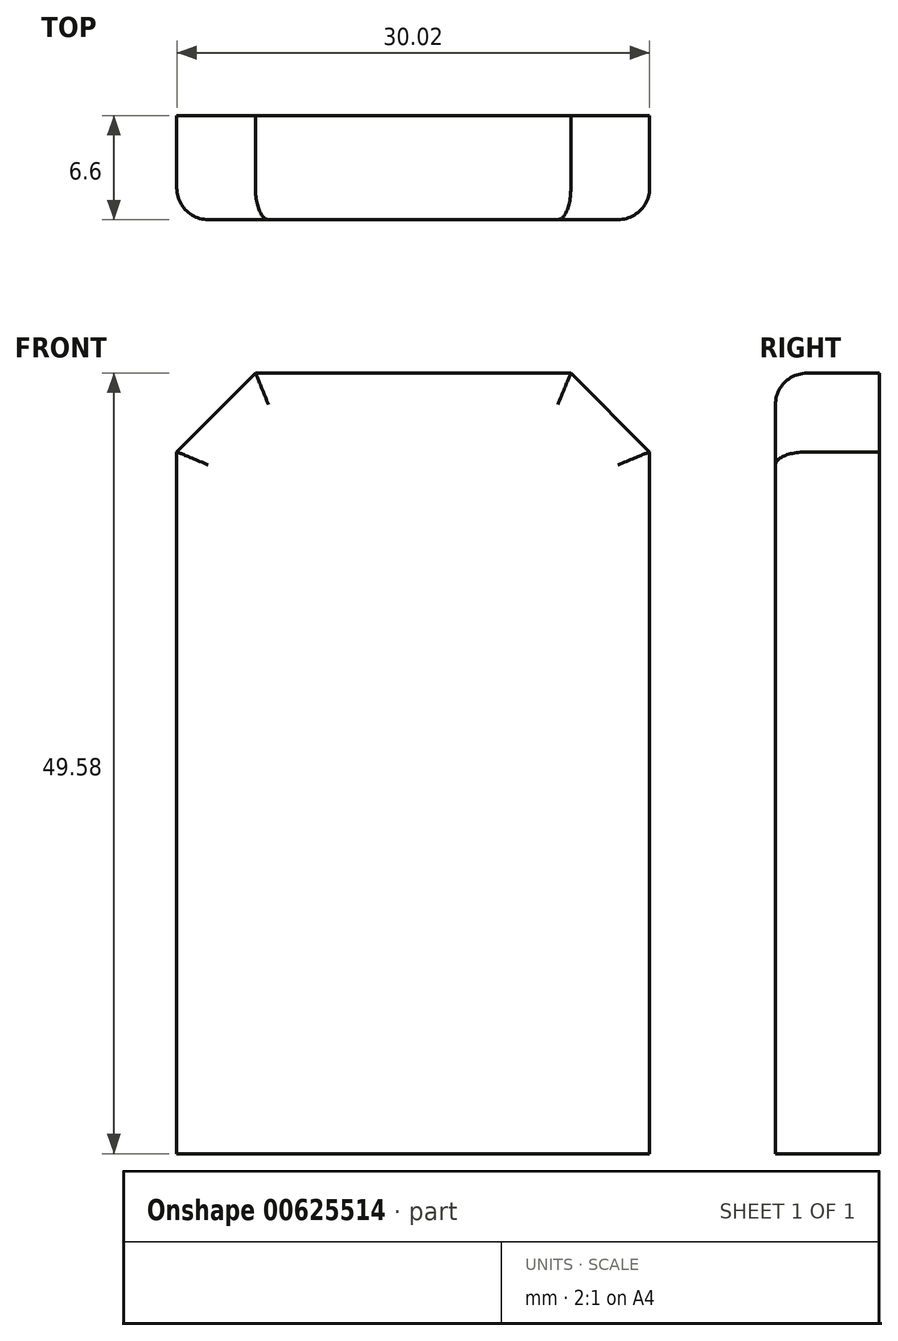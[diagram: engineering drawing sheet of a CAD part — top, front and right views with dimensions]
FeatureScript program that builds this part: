
annotation { "Feature Type Name" : "Feature", "Feature Type Description" : "" }
export const myFeature = defineFeature(function(context is Context, id is Id, definition is map)
    precondition{}
    {
        {
            var Q0;
            Q0=qCreatedBy(makeId("Front.planeOp"),FACE);
            var sketch = newSketch(context, id + "F0", { "sketchPlane" : qUnion([Q0])});
            skLineSegment(sketch, "E0.bottom", {"start": v(15.01, -24.79) * mm, "end": v(-15.01, -24.79) * mm});
            skLineSegment(sketch, "E0.top", {"start": v(15.01, 24.79) * mm, "end": v(-15.01, 24.79) * mm});
            skLineSegment(sketch, "E0.left", {"start": v(15.01, -24.79) * mm, "end": v(15.01, 24.79) * mm});
            skLineSegment(sketch, "E0.right", {"start": v(-15.01, -24.79) * mm, "end": v(-15.01, 24.79) * mm});
            skPoint(sketch, "E0.middle", {"position": v(0, 0) * mm});
            skSolve(sketch);
        }
        {
            var Q0;
            Q0 = qSketchRegion(id + "F0", true);
            extrude(context, id + "F1", {"entities" : qUnion([Q0]), "depth" : 6.6 * mm, "offsetDistance" : 25 * mm});
        }
        {
            var Q0;
            Q0=makeQuery(id+"F1.opExtrude","SWEPT_EDGE",EDGE,{"disambiguationData":[OSD([sQuery(id+"F0.wireOp",EDGE,"E0.top"),sQuery(id+"F0.wireOp",EDGE,"E0.right")])]});
            var Q1;
            Q1=makeQuery(id+"F1.opExtrude","SWEPT_EDGE",EDGE,{"disambiguationData":[OSD([sQuery(id+"F0.wireOp",EDGE,"E0.top"),sQuery(id+"F0.wireOp",EDGE,"E0.left")])]});
            chamfer(context, id + "F2", {"entities" : qUnion([Q0, Q1]), "width" : 5 * mm, "tangentPropagation" : true});
        }
        {
            var Q0;
            {var subQ0=sQuery(id+"F0.wireOp",EDGE,"E0.left");var subQ1=sQuery(id+"F0.wireOp",EDGE,"E0.top");Q0=makeQuery(id+"F2.opChamfer","BLEND_EDGE",EDGE,{"blendedFrom":[makeQuery(id+"F1.opExtrude","SWEPT_EDGE",EDGE,{"disambiguationData":[OSD([subQ1,subQ0])]}),makeQuery(id+"F1.opExtrude","CAP_FACE",FACE,{"disambiguationData":[OSD([sQuery(id+"F0.wireOp",EDGE,"E0.bottom"),subQ1,subQ0,sQuery(id+"F0.wireOp",EDGE,"E0.right")])],"isStart":false})],"blendedInto":[makeQuery(id+"F1.opExtrude","CAP_FACE",FACE,{"disambiguationData":[OSD([sQuery(id+"F0.wireOp",EDGE,"E0.bottom"),subQ1,subQ0,sQuery(id+"F0.wireOp",EDGE,"E0.right")])],"isStart":false})]});}
            var Q1;
            Q1=makeQuery(id+"F1.opExtrude","CAP_EDGE",EDGE,{"disambiguationData":[OSD([sQuery(id+"F0.wireOp",EDGE,"E0.right")])],"isStart":false});
            var Q2;
            Q2=makeQuery(id+"F1.opExtrude","CAP_EDGE",EDGE,{"disambiguationData":[OSD([sQuery(id+"F0.wireOp",EDGE,"E0.top")])],"isStart":false});
            var Q3;
            Q3=makeQuery(id+"F1.opExtrude","CAP_EDGE",EDGE,{"disambiguationData":[OSD([sQuery(id+"F0.wireOp",EDGE,"E0.left")])],"isStart":false});
            var Q4;
            {var subQ0=sQuery(id+"F0.wireOp",EDGE,"E0.right");var subQ1=sQuery(id+"F0.wireOp",EDGE,"E0.top");Q4=makeQuery(id+"F2.opChamfer","BLEND_EDGE",EDGE,{"blendedFrom":[makeQuery(id+"F1.opExtrude","SWEPT_EDGE",EDGE,{"disambiguationData":[OSD([subQ1,subQ0])]}),makeQuery(id+"F1.opExtrude","CAP_FACE",FACE,{"disambiguationData":[OSD([sQuery(id+"F0.wireOp",EDGE,"E0.bottom"),subQ1,sQuery(id+"F0.wireOp",EDGE,"E0.left"),subQ0])],"isStart":false})],"blendedInto":[makeQuery(id+"F1.opExtrude","CAP_FACE",FACE,{"disambiguationData":[OSD([sQuery(id+"F0.wireOp",EDGE,"E0.bottom"),subQ1,sQuery(id+"F0.wireOp",EDGE,"E0.left"),subQ0])],"isStart":false})]});}
            fillet(context, id + "F3", {"entities" : qUnion([Q0, Q1, Q2, Q3, Q4]), "radius" : 2 * mm, "tangentPropagation" : true, "allowEdgeOverflow" : false});
        }
    });
